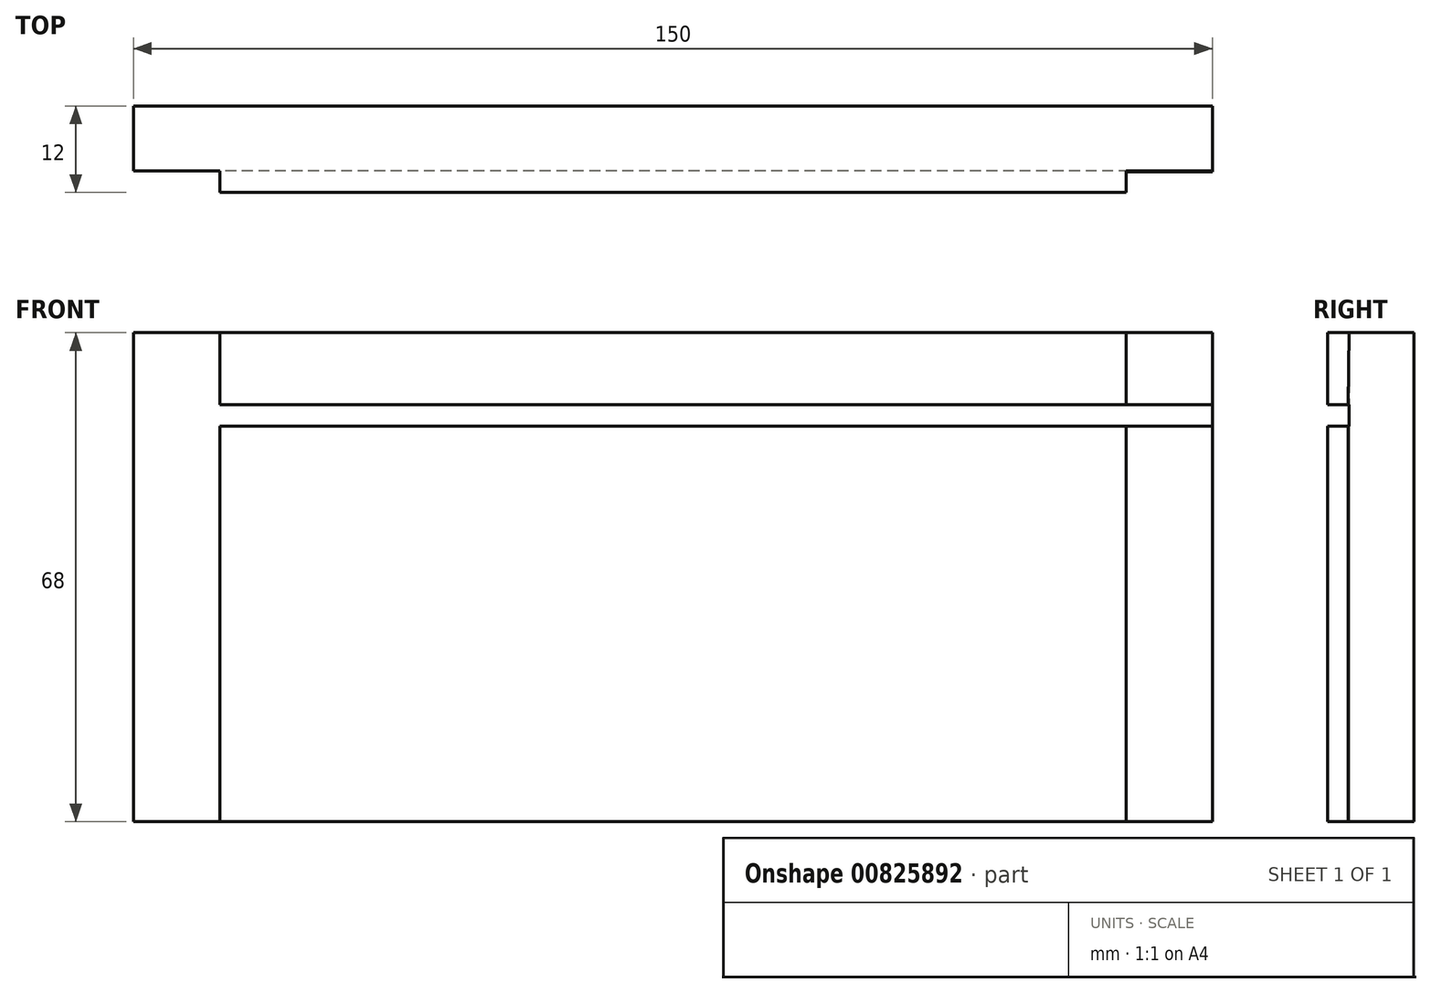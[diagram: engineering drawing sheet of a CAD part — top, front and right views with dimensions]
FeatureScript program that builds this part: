
annotation { "Feature Type Name" : "Feature", "Feature Type Description" : "" }
export const myFeature = defineFeature(function(context is Context, id is Id, definition is map)
    precondition{}
    {
        {
            var Q0;
            Q0=qCreatedBy(makeId("Right.planeOp"),FACE);
            var sketch = newSketch(context, id + "F0", { "sketchPlane" : qUnion([Q0])});
            skLineSegment(sketch, "E0.bottom", {"start": v(6, -34) * mm, "end": v(-6, -34) * mm});
            skLineSegment(sketch, "E0.top", {"start": v(6, 34) * mm, "end": v(-6, 34) * mm});
            skLineSegment(sketch, "E0.left", {"start": v(6, -34) * mm, "end": v(6, 34) * mm});
            skLineSegment(sketch, "E0.right", {"start": v(-6, -34) * mm, "end": v(-6, 34) * mm});
            skPoint(sketch, "E0.middle", {"position": v(0, 0) * mm});
            skLineSegment(sketch, "E1", {"start": v(-6, 24) * mm, "end": v(-3, 24) * mm});
            skLineSegment(sketch, "E2", {"start": v(-3, 24) * mm, "end": v(-3, 21) * mm});
            skLineSegment(sketch, "E3", {"start": v(-3, 21) * mm, "end": v(-6, 21) * mm});
            skSolve(sketch);
        }
        {
            var Q0;
            {var subQ1=sQuery(id+"F0.wireOp",EDGE,"E0.bottom");Q0=makeQuery(id+"F0.imprint","IMPRINT",FACE,{"disambiguationData":[TD([[makeQuery(id+"F0.imprint","IMPRINT",EDGE,{"derivedFrom":subQ1}),-1.0]])]});}
            extrude(context, id + "F1", {"entities" : qUnion([Q0]), "endBound" : BoundingType.SYMMETRIC, "depth" : 150 * mm, "offsetDistance" : 25.4 * mm});
        }
        {
            var Q0;
            Q0=makeQuery(id+"F1.opExtrude","CAP_FACE",FACE,{"disambiguationData":[OSD([sQuery(id+"F0.wireOp",EDGE,"E0.bottom"),sQuery(id+"F0.wireOp",EDGE,"E0.top"),sQuery(id+"F0.wireOp",EDGE,"E0.left"),sQuery(id+"F0.wireOp",EDGE,"E0.right"),sQuery(id+"F0.wireOp",EDGE,"E1"),sQuery(id+"F0.wireOp",EDGE,"E2"),sQuery(id+"F0.wireOp",EDGE,"E3")])],"isStart":false});
            var sketch = newSketch(context, id + "F2", { "sketchPlane" : qUnion([Q0])});
            skLineSegment(sketch, "E4", {"start": v(-3.16, 34) * mm, "end": v(-3.16, -34) * mm});
            skPoint(sketch, "E4.endSnap0", {"position": v(0, -34) * mm});
            skSolve(sketch);
        }
        {
            var Q0;
            {var subQ1=sQuery(id+"F0.wireOp",EDGE,"E0.bottom");var subQ7=sQuery(id+"F0.wireOp",EDGE,"E0.right");var subQ8=makeQuery(id+"F1.opExtrude","CAP_EDGE",EDGE,{"disambiguationData":[OSD([subQ7]),TDD([makeQuery(id+"F0.imprint","IMPRINT",EDGE,{"disambiguationData":[TD([[makeQuery(id+"F0.imprint","INTERSECT",VERTEX,{"derivedFrom":[subQ1,subQ7]}),-1.0]])],"derivedFrom":subQ7})])],"isStart":false});Q0=makeQuery(id+"F2.imprint","IMPRINT",FACE,{"disambiguationData":[TD([[makeQuery(id+"F2.imprint","IMPRINT",EDGE,{"derivedFrom":subQ8}),-1.0]])]});}
            extrude(context, id + "F3", {"entities" : qUnion([Q0]), "operationType" : NewBodyOperationType.REMOVE, "oppositeDirection" : true, "depth" : 12 * mm, "offsetDistance" : 25.4 * mm});
        }
        {
            var Q0;
            Q0=makeQuery(id+"F1.opExtrude","CAP_FACE",FACE,{"disambiguationData":[OSD([sQuery(id+"F0.wireOp",EDGE,"E0.bottom"),sQuery(id+"F0.wireOp",EDGE,"E0.top"),sQuery(id+"F0.wireOp",EDGE,"E0.left"),sQuery(id+"F0.wireOp",EDGE,"E0.right"),sQuery(id+"F0.wireOp",EDGE,"E1"),sQuery(id+"F0.wireOp",EDGE,"E2"),sQuery(id+"F0.wireOp",EDGE,"E3")])],"isStart":false});
            var sketch = newSketch(context, id + "F4", { "sketchPlane" : qUnion([Q0])});
            skLineSegment(sketch, "E5", {"start": v(-3.16, 18.25) * mm, "end": v(-3, 34) * mm});
            skSolve(sketch);
        }
        {
            var Q0;
            {var subQ1=sQuery(id+"F0.wireOp",EDGE,"E0.top");var subQ7=sQuery(id+"F0.wireOp",EDGE,"E0.right");var subQ8=makeQuery(id+"F1.opExtrude","CAP_EDGE",EDGE,{"disambiguationData":[OSD([subQ7]),TDD([makeQuery(id+"F0.imprint","IMPRINT",EDGE,{"disambiguationData":[TD([[makeQuery(id+"F0.imprint","INTERSECT",VERTEX,{"derivedFrom":[subQ1,subQ7]}),1.0]])],"derivedFrom":subQ7})])],"isStart":false});Q0=makeQuery(id+"F4.imprint","IMPRINT",FACE,{"disambiguationData":[TD([[makeQuery(id+"F4.imprint","IMPRINT",EDGE,{"derivedFrom":subQ8}),-1.0]])]});}
            extrude(context, id + "F5", {"entities" : qUnion([Q0]), "operationType" : NewBodyOperationType.REMOVE, "oppositeDirection" : true, "depth" : 12 * mm, "offsetDistance" : 25.4 * mm});
        }
        {
            var Q0;
            Q0=makeQuery(id+"F1.opExtrude","CAP_FACE",FACE,{"disambiguationData":[OSD([sQuery(id+"F0.wireOp",EDGE,"E0.bottom"),sQuery(id+"F0.wireOp",EDGE,"E0.top"),sQuery(id+"F0.wireOp",EDGE,"E0.left"),sQuery(id+"F0.wireOp",EDGE,"E0.right"),sQuery(id+"F0.wireOp",EDGE,"E1"),sQuery(id+"F0.wireOp",EDGE,"E2"),sQuery(id+"F0.wireOp",EDGE,"E3")])],"isStart":true});
            var sketch = newSketch(context, id + "F6", { "sketchPlane" : qUnion([Q0])});
            skLineSegment(sketch, "E6", {"start": v(3, 24) * mm, "end": v(3, 34) * mm});
            skLineSegment(sketch, "E7", {"start": v(3, 34) * mm, "end": v(3, -34) * mm});
            skSolve(sketch);
        }
        {
            var Q0;
            {var subQ1=sQuery(id+"F0.wireOp",EDGE,"E3");var subQ2=makeQuery(id+"F1.opExtrude","CAP_EDGE",EDGE,{"disambiguationData":[OSD([subQ1])],"isStart":true});Q0=makeQuery(id+"F6.imprint","IMPRINT",FACE,{"disambiguationData":[TD([[makeQuery(id+"F6.imprint","IMPRINT",EDGE,{"derivedFrom":subQ2}),-1.0]])]});}
            var Q1;
            {var subQ1=sQuery(id+"F0.wireOp",EDGE,"E1");var subQ2=makeQuery(id+"F1.opExtrude","CAP_EDGE",EDGE,{"disambiguationData":[OSD([subQ1])],"isStart":true});Q1=makeQuery(id+"F6.imprint","IMPRINT",FACE,{"disambiguationData":[TD([[makeQuery(id+"F6.imprint","IMPRINT",EDGE,{"derivedFrom":subQ2}),-1.0]])]});}
            extrude(context, id + "F7", {"entities" : qUnion([Q0, Q1]), "operationType" : NewBodyOperationType.REMOVE, "oppositeDirection" : true, "depth" : 12 * mm, "offsetDistance" : 25.4 * mm});
        }
    });
